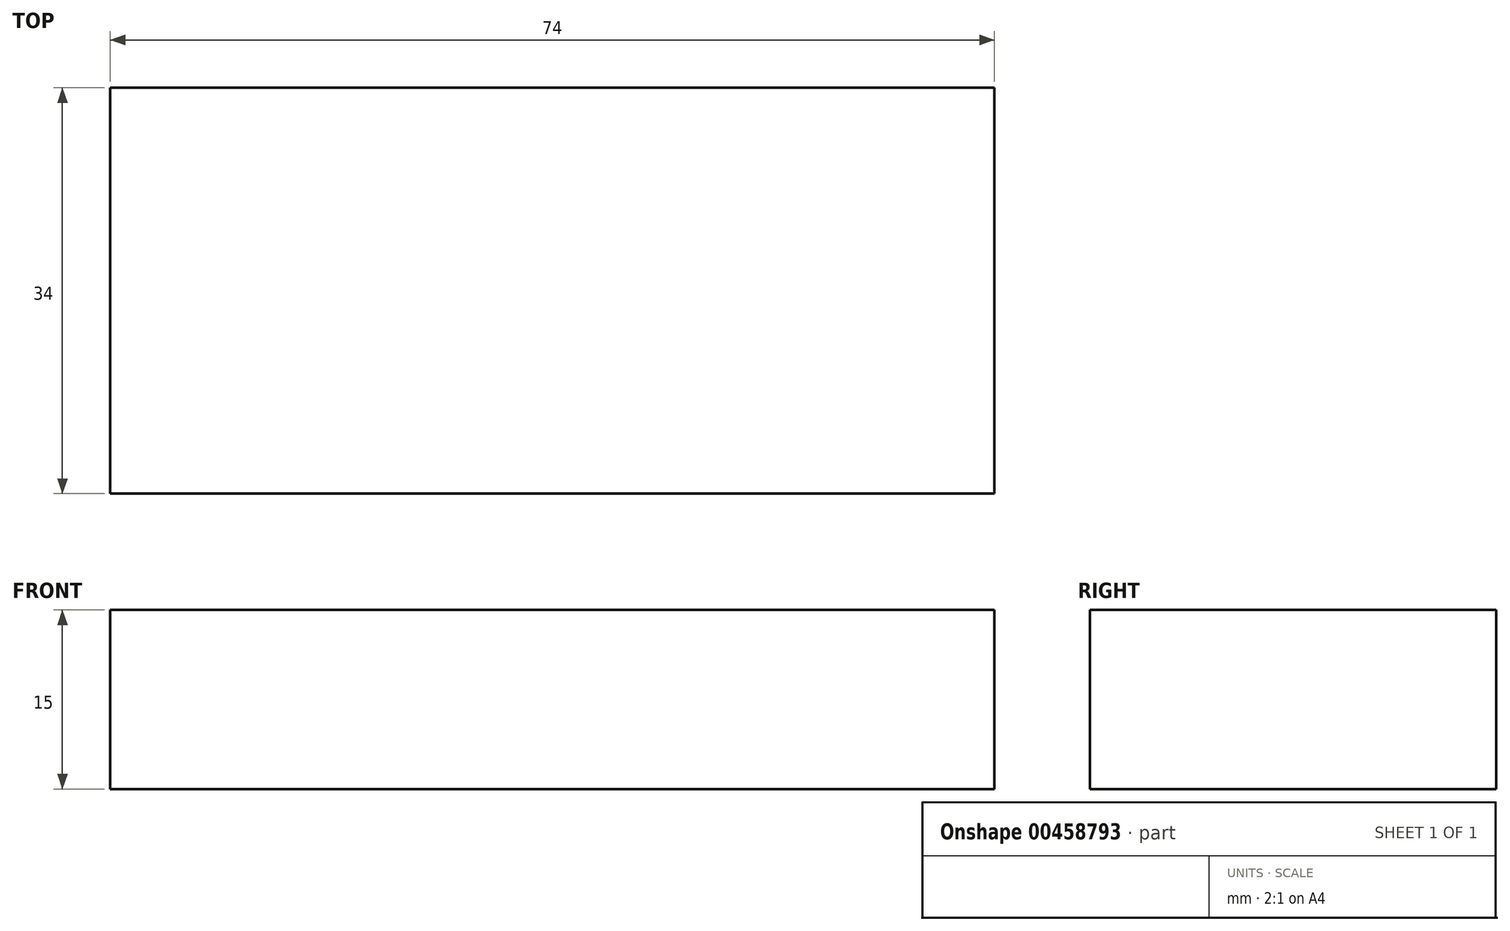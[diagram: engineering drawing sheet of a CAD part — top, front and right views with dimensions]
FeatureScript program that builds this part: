
annotation { "Feature Type Name" : "Feature", "Feature Type Description" : "" }
export const myFeature = defineFeature(function(context is Context, id is Id, definition is map)
    precondition{}
    {
        {
            var Q0;
            Q0=qCreatedBy(makeId("Top.planeOp"),FACE);
            var sketch = newSketch(context, id + "F0", { "sketchPlane" : qUnion([Q0])});
            skLineSegment(sketch, "E0.bottom", {"start": v(-35.88, 14.57) * mm, "end": v(38.12, 14.57) * mm});
            skLineSegment(sketch, "E0.top", {"start": v(-35.88, -19.43) * mm, "end": v(38.12, -19.43) * mm});
            skLineSegment(sketch, "E0.left", {"start": v(-35.88, 14.57) * mm, "end": v(-35.88, -19.43) * mm});
            skLineSegment(sketch, "E0.right", {"start": v(38.12, 14.57) * mm, "end": v(38.12, -19.43) * mm});
            skSolve(sketch);
        }
        {
            var Q0;
            Q0=makeQuery(id+"F0.imprint","IMPRINT",FACE,{"disambiguationData":[TD([[makeQuery(id+"F0.imprint","IMPRINT",EDGE,{"derivedFrom":sQuery(id+"F0.wireOp",EDGE,"E0.bottom")}),-1.0]])]});
            extrude(context, id + "F1", {"entities" : qUnion([Q0]), "depth" : 15 * mm, "offsetDistance" : 25 * mm, "symmetric" : true});
        }
    });
